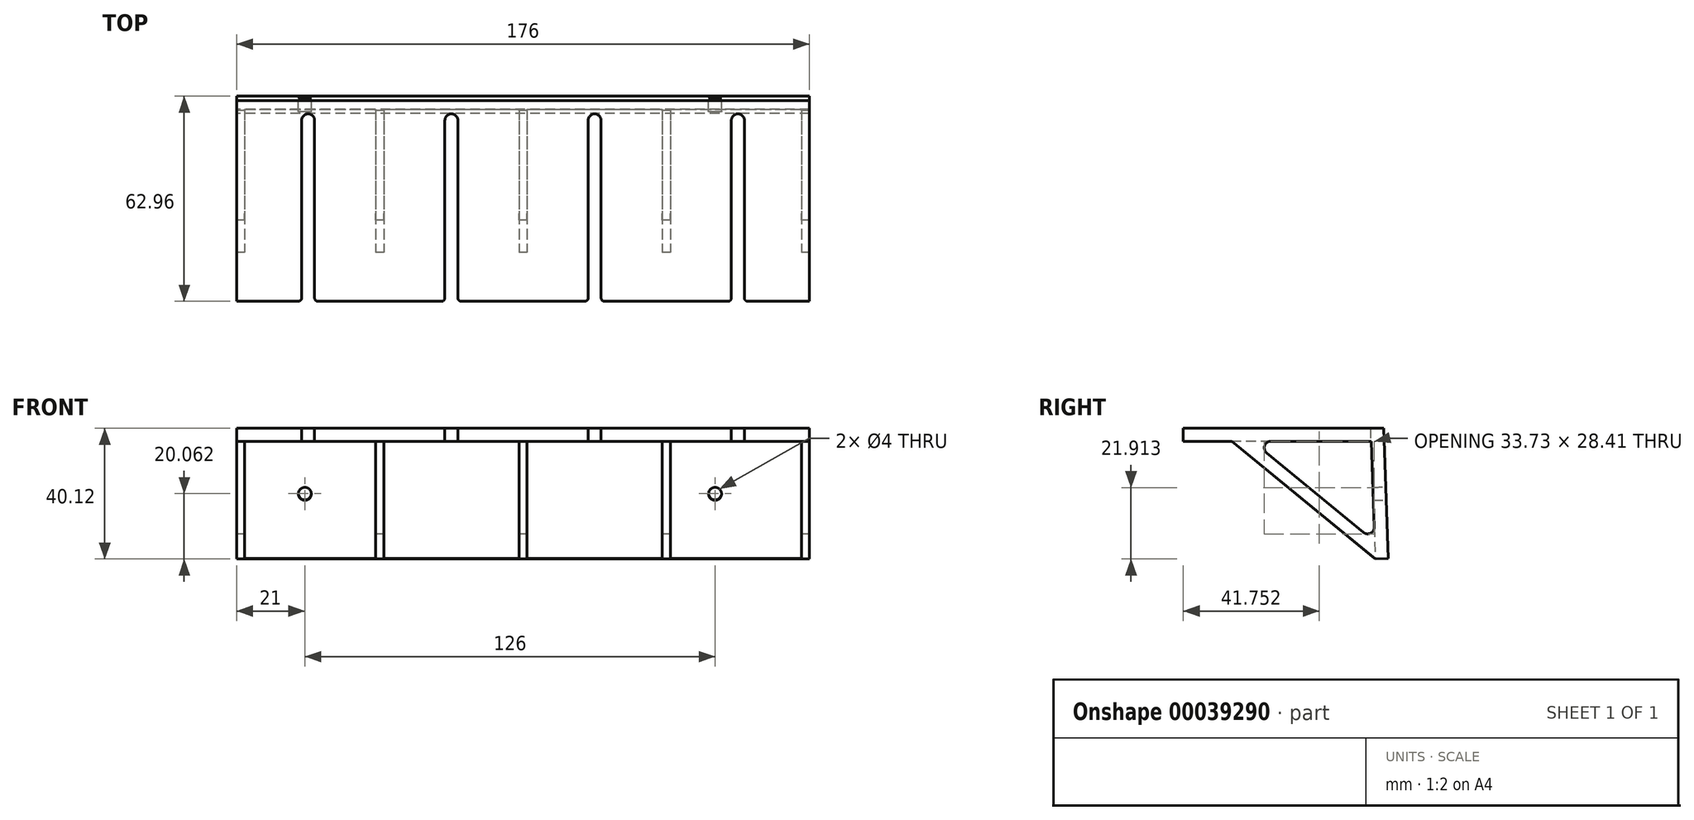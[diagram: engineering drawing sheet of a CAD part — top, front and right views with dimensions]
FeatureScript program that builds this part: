
annotation { "Feature Type Name" : "Feature", "Feature Type Description" : "" }
export const myFeature = defineFeature(function(context is Context, id is Id, definition is map)
    precondition{}
    {
        {
            var Q0;
            Q0=qCreatedBy(makeId("Top.planeOp"),FACE);
            var sketch = newSketch(context, id + "F0", { "sketchPlane" : qUnion([Q0])});
            skLineSegment(sketch, "E0", {"start": v(0, 0) * mm, "end": v(176, 0) * mm});
            skLineSegment(sketch, "E1", {"start": v(0, 0) * mm, "end": v(0, -61.56) * mm});
            skLineSegment(sketch, "E2", {"start": v(0, -61.56) * mm, "end": v(19, -61.56) * mm});
            skLineSegment(sketch, "E3", {"start": v(20, -60.56) * mm, "end": v(20, -6) * mm});
            skLineSegment(sketch, "E4", {"start": v(24, -6) * mm, "end": v(24, -60.56) * mm});
            skLineSegment(sketch, "E5", {"start": v(25, -61.56) * mm, "end": v(63, -61.56) * mm});
            skLineSegment(sketch, "E6", {"start": v(64, -60.56) * mm, "end": v(64, -6) * mm});
            skLineSegment(sketch, "E7", {"start": v(68, -6) * mm, "end": v(68, -60.56) * mm});
            skLineSegment(sketch, "E8", {"start": v(69, -61.56) * mm, "end": v(107, -61.56) * mm});
            skLineSegment(sketch, "E9", {"start": v(108, -60.56) * mm, "end": v(108, -6) * mm});
            skLineSegment(sketch, "E10", {"start": v(112, -6) * mm, "end": v(112, -60.56) * mm});
            skLineSegment(sketch, "E11", {"start": v(113, -61.56) * mm, "end": v(151, -61.56) * mm});
            skLineSegment(sketch, "E12", {"start": v(152, -60.56) * mm, "end": v(152, -6) * mm});
            skLineSegment(sketch, "E13", {"start": v(156, -6) * mm, "end": v(156, -60.56) * mm});
            skArc(sketch, "E14", {"start": v(20, -6) * mm, "mid": v(22, -4) * mm, "end": v(24, -6) * mm});
            skArc(sketch, "E15", {"start": v(64, -6) * mm, "mid": v(66, -4) * mm, "end": v(68, -6) * mm});
            skArc(sketch, "E16", {"start": v(108, -6) * mm, "mid": v(110, -4) * mm, "end": v(112, -6) * mm});
            skArc(sketch, "E17", {"start": v(152, -6) * mm, "mid": v(154, -4) * mm, "end": v(156, -6) * mm});
            skLineSegment(sketch, "E18", {"start": v(22, -6) * mm, "end": v(154, -6) * mm, "construction": true});
            skPoint(sketch, "E19.visualSharp", {"position": v(64, -61.56) * mm});
            skArc(sketch, "E19.filletArc", {"start": v(63, -61.56) * mm, "mid": v(63.7, -61.27) * mm, "end": v(64, -60.56) * mm});
            skPoint(sketch, "E20.visualSharp", {"position": v(20, -61.56) * mm});
            skArc(sketch, "E20.filletArc", {"start": v(19, -61.56) * mm, "mid": v(19.7, -61.27) * mm, "end": v(20, -60.56) * mm});
            skPoint(sketch, "E21.visualSharp", {"position": v(24, -61.56) * mm});
            skArc(sketch, "E21.filletArc", {"start": v(24, -60.56) * mm, "mid": v(24.3, -61.27) * mm, "end": v(25, -61.56) * mm});
            skPoint(sketch, "E22.visualSharp", {"position": v(68, -61.56) * mm});
            skArc(sketch, "E22.filletArc", {"start": v(68, -60.56) * mm, "mid": v(68.3, -61.27) * mm, "end": v(69, -61.56) * mm});
            skPoint(sketch, "E23.visualSharp", {"position": v(108, -61.56) * mm});
            skArc(sketch, "E23.filletArc", {"start": v(107, -61.56) * mm, "mid": v(107.7, -61.27) * mm, "end": v(108, -60.56) * mm});
            skPoint(sketch, "E24.visualSharp", {"position": v(112, -61.56) * mm});
            skArc(sketch, "E24.filletArc", {"start": v(112, -60.56) * mm, "mid": v(112.3, -61.27) * mm, "end": v(113, -61.56) * mm});
            skPoint(sketch, "E25.visualSharp", {"position": v(152, -61.56) * mm});
            skArc(sketch, "E25.filletArc", {"start": v(151, -61.56) * mm, "mid": v(151.7, -61.27) * mm, "end": v(152, -60.56) * mm});
            skLineSegment(sketch, "E26", {"start": v(157, -61.56) * mm, "end": v(176, -61.56) * mm});
            skLineSegment(sketch, "E27", {"start": v(176, -61.56) * mm, "end": v(176, 0) * mm});
            skPoint(sketch, "E28.visualSharp", {"position": v(156, -61.56) * mm});
            skArc(sketch, "E28.filletArc", {"start": v(156, -60.56) * mm, "mid": v(156.3, -61.27) * mm, "end": v(157, -61.56) * mm});
            skSolve(sketch);
        }
        {
            var Q0;
            Q0=makeQuery(id+"F0.imprint","IMPRINT",FACE,{"disambiguationData":[TD([[makeQuery(id+"F0.imprint","IMPRINT",EDGE,{"derivedFrom":sQuery(id+"F0.wireOp",EDGE,"E0")}),-1.0]])]});
            extrude(context, id + "F1", {"entities" : qUnion([Q0]), "depth" : 4 * mm});
        }
        {
            var Q0;
            Q0=makeQuery(id+"F1.opExtrude","SWEPT_FACE",FACE,{"disambiguationData":[OSD([sQuery(id+"F0.wireOp",EDGE,"E0")])]});
            var sketch = newSketch(context, id + "F2", { "sketchPlane" : qUnion([Q0])});
            skLineSegment(sketch, "E29", {"start": v(0, 4) * mm, "end": v(0, -100) * mm});
            skLineSegment(sketch, "E30", {"start": v(0, -100) * mm, "end": v(-44, -100) * mm});
            skLineSegment(sketch, "E31", {"start": v(-44, -110) * mm, "end": v(-44, -100) * mm});
            skLineSegment(sketch, "E32", {"start": v(-44, -110) * mm, "end": v(-88, -110) * mm});
            skLineSegment(sketch, "E33", {"start": v(-88, -135) * mm, "end": v(-88, -110) * mm});
            skLineSegment(sketch, "E34", {"start": v(-88, -135) * mm, "end": v(-132, -135) * mm});
            skLineSegment(sketch, "E35", {"start": v(-132, -155) * mm, "end": v(-132, -135) * mm});
            skLineSegment(sketch, "E36", {"start": v(-132, -155) * mm, "end": v(-176, -155) * mm});
            skLineSegment(sketch, "E37", {"start": v(-176, -155) * mm, "end": v(-176, -22) * mm});
            skLineSegment(sketch, "E38", {"start": v(-154, 4) * mm, "end": v(-154, -155) * mm, "construction": true});
            skLineSegment(sketch, "E39", {"start": v(-110, -135) * mm, "end": v(-110, 4) * mm, "construction": true});
            skLineSegment(sketch, "E40", {"start": v(-66, -110) * mm, "end": v(-66, 4) * mm, "construction": true});
            skLineSegment(sketch, "E41", {"start": v(-22, -100) * mm, "end": v(-22, 4) * mm, "construction": true});
            skLineSegment(sketch, "E42", {"start": v(-22, -48.08) * mm, "end": v(-66, -48.08) * mm, "construction": true});
            skLineSegment(sketch, "E43", {"start": v(-66, -48.08) * mm, "end": v(-110, -48.08) * mm, "construction": true});
            skLineSegment(sketch, "E44", {"start": v(-110, -48.08) * mm, "end": v(-154, -48.08) * mm, "construction": true});
            skLineSegment(sketch, "E45", {"start": v(-132, -135) * mm, "end": v(-132, -48.08) * mm, "construction": true});
            skLineSegment(sketch, "E46", {"start": v(-88, -110) * mm, "end": v(-88, -48.08) * mm, "construction": true});
            skLineSegment(sketch, "E47", {"start": v(-44, -100) * mm, "end": v(-44, -48.08) * mm, "construction": true});
            skLineSegment(sketch, "E48", {"start": v(0, 4) * mm, "end": v(-176, 4) * mm});
            skLineSegment(sketch, "E49", {"start": v(-176, 4) * mm, "end": v(-304, 4) * mm});
            skLineSegment(sketch, "E50", {"start": v(-304, 4) * mm, "end": v(-304, -22) * mm});
            skLineSegment(sketch, "E51", {"start": v(-304, -22) * mm, "end": v(-176, -22) * mm});
            skCircle(sketch, "E52", {"center": v(-195, -9) * mm, "radius": 9 * mm});
            skCircle(sketch, "E53", {"center": v(-243, -9) * mm, "radius": 9 * mm});
            skCircle(sketch, "E54", {"center": v(-291, -9) * mm, "radius": 9 * mm});
            skLineSegment(sketch, "E55", {"start": v(-195, -9) * mm, "end": v(-291, -9) * mm, "construction": true});
            skLineSegment(sketch, "E56", {"start": v(-291, -9) * mm, "end": v(-304, -9) * mm, "construction": true});
            skLineSegment(sketch, "E57", {"start": v(-176, -22) * mm, "end": v(-176, 4) * mm});
            skSolve(sketch);
        }
        {
            var Q0;
            Q0=makeQuery(id+"F1.opExtrude","SWEPT_FACE",FACE,{"disambiguationData":[OSD([sQuery(id+"F0.wireOp",EDGE,"E1")])]});
            var sketch = newSketch(context, id + "F3", { "sketchPlane" : qUnion([Q0])});
            skLineSegment(sketch, "E58", {"start": v(3.86, 0) * mm, "end": v(34.67, 0) * mm});
            skLineSegment(sketch, "E59", {"start": v(0, 4) * mm, "end": v(-1.4, -35.98) * mm});
            skLineSegment(sketch, "E60", {"start": v(2.94, -26.36) * mm, "end": v(3.86, 0) * mm});
            skLineSegment(sketch, "E61", {"start": v(0, 4) * mm, "end": v(4, 4) * mm});
            skLineSegment(sketch, "E62", {"start": v(2.6, -36.12) * mm, "end": v(-1.4, -35.98) * mm});
            skLineSegment(sketch, "E63", {"start": v(46.56, 0) * mm, "end": v(2.6, -36.12) * mm});
            skLineSegment(sketch, "E64.0", {"start": v(35.94, -3.55) * mm, "end": v(6.21, -27.97) * mm});
            skPoint(sketch, "E65.visualSharp", {"position": v(2.79, -30.79) * mm});
            skArc(sketch, "E65.filletArc", {"start": v(2.94, -26.36) * mm, "mid": v(4.06, -28.22) * mm, "end": v(6.21, -27.97) * mm});
            skPoint(sketch, "E66.visualSharp", {"position": v(40.26, 0) * mm});
            skArc(sketch, "E66.filletArc", {"start": v(35.94, -3.55) * mm, "mid": v(36.56, -1.33) * mm, "end": v(34.67, 0) * mm});
            skPoint(sketch, "E67.visualSharp", {"position": v(3.86, 0) * mm});
            skSolve(sketch);
        }
        {
            var Q0;
            Q0=makeQuery(id+"F3.imprint","IMPRINT",FACE,{"disambiguationData":[TD([[makeQuery(id+"F3.imprint","IMPRINT",EDGE,{"derivedFrom":sQuery(id+"F3.wireOp",EDGE,"E59")}),1.0]])]});
            var Q1;
            Q1=makeQuery(id+"F3.imprint","IMPRINT",FACE,{"disambiguationData":[TD([[makeQuery(id+"F3.imprint","IMPRINT",EDGE,{"derivedFrom":sQuery(id+"F3.wireOp",EDGE,"c7156f05-824d-4470-9329-524be284baaa")}),-1.0]])]});
            var Q2;
            Q2=makeQuery(id+"F1.opExtrude","SWEPT_FACE",FACE,{"disambiguationData":[OSD([sQuery(id+"F0.wireOp",EDGE,"E27")])]});
            extrude(context, id + "F4", {"entities" : qUnion([Q0, Q1]), "operationType" : NewBodyOperationType.ADD, "endBound" : BoundingType.UP_TO_SURFACE, "oppositeDirection" : true, "endBoundEntityFace" : qUnion([Q2]), "depth" : 2.5 * mm});
        }
        {
            var Q0;
            Q0=makeQuery(id+"F4.opExtrude","SWEPT_FACE",FACE,{"disambiguationData":[OSD([sQuery(id+"F3.wireOp",EDGE,"E59")])]});
            cPlane(context, id + "F5", {"entities" : qUnion([Q0]), "cplaneType" : CPlaneType.OFFSET, "offset" : 4 * mm, "oppositeDirection" : true, "width" : 150 * mm, "height" : 150 * mm});
        }
        {
            var Q0;
            Q0=makeQuery(id+"F1.opExtrude","SWEPT_FACE",FACE,{"disambiguationData":[OSD([sQuery(id+"F0.wireOp",EDGE,"E2")])]});
            var sketch = newSketch(context, id + "F6", { "sketchPlane" : qUnion([Q0])});
            skLineSegment(sketch, "E68.bottom", {"start": v(2.5, 0) * mm, "end": v(42.75, 0) * mm});
            skLineSegment(sketch, "E68.top", {"start": v(2.5, -35.98) * mm, "end": v(42.75, -35.98) * mm});
            skLineSegment(sketch, "E68.left", {"start": v(2.5, 0) * mm, "end": v(2.5, -35.98) * mm});
            skLineSegment(sketch, "E68.right", {"start": v(42.75, 0) * mm, "end": v(42.75, -35.98) * mm});
            skLineSegment(sketch, "E69.bottom", {"start": v(45.25, 0) * mm, "end": v(86.75, 0) * mm});
            skLineSegment(sketch, "E69.top", {"start": v(45.25, -35.98) * mm, "end": v(86.75, -35.98) * mm});
            skLineSegment(sketch, "E69.left", {"start": v(45.25, 0) * mm, "end": v(45.25, -35.98) * mm});
            skLineSegment(sketch, "E69.right", {"start": v(86.75, 0) * mm, "end": v(86.75, -35.98) * mm});
            skLineSegment(sketch, "E70.bottom", {"start": v(89.25, 0) * mm, "end": v(130.75, 0) * mm});
            skLineSegment(sketch, "E70.top", {"start": v(89.25, -35.98) * mm, "end": v(130.75, -35.98) * mm});
            skLineSegment(sketch, "E70.left", {"start": v(89.25, 0) * mm, "end": v(89.25, -35.98) * mm});
            skLineSegment(sketch, "E70.right", {"start": v(130.75, 0) * mm, "end": v(130.75, -35.98) * mm});
            skLineSegment(sketch, "E71.bottom", {"start": v(133.25, 0) * mm, "end": v(173.5, 0) * mm});
            skLineSegment(sketch, "E71.top", {"start": v(133.25, -35.98) * mm, "end": v(173.5, -35.98) * mm});
            skLineSegment(sketch, "E71.left", {"start": v(133.25, 0) * mm, "end": v(133.25, -35.98) * mm});
            skLineSegment(sketch, "E71.right", {"start": v(173.5, 0) * mm, "end": v(173.5, -35.98) * mm});
            skLineSegment(sketch, "E72", {"start": v(42.75, -35.98) * mm, "end": v(45.25, -35.98) * mm, "construction": true});
            skLineSegment(sketch, "E73", {"start": v(86.75, -35.98) * mm, "end": v(89.25, -35.98) * mm, "construction": true});
            skLineSegment(sketch, "E74", {"start": v(130.75, -35.98) * mm, "end": v(133.25, -35.98) * mm, "construction": true});
            skLineSegment(sketch, "E75", {"start": v(44, -35.98) * mm, "end": v(44, -100) * mm, "construction": true});
            skSolve(sketch);
        }
        {
            var Q0;
            {Q0=qUnion([makeQuery(id+"F6.imprint","IMPRINT",FACE,{"disambiguationData":[TD([[makeQuery(id+"F6.imprint","IMPRINT",EDGE,{"derivedFrom":sQuery(id+"F6.wireOp",EDGE,"E71.bottom")}),-1.0]])]}),makeQuery(id+"F6.imprint","IMPRINT",FACE,{"disambiguationData":[TD([[makeQuery(id+"F6.imprint","IMPRINT",EDGE,{"derivedFrom":sQuery(id+"F6.wireOp",EDGE,"E70.bottom")}),-1.0]])]}),makeQuery(id+"F6.imprint","IMPRINT",FACE,{"disambiguationData":[TD([[makeQuery(id+"F6.imprint","IMPRINT",EDGE,{"derivedFrom":sQuery(id+"F6.wireOp",EDGE,"E69.bottom")}),-1.0]])]}),makeQuery(id+"F6.imprint","IMPRINT",FACE,{"disambiguationData":[TD([[makeQuery(id+"F6.imprint","IMPRINT",EDGE,{"derivedFrom":sQuery(id+"F6.wireOp",EDGE,"E68.top")}),1.0]])]})]);}
            var Q1;
            Q1=qCreatedBy(id+"F5.planeOp",FACE);
            extrude(context, id + "F7", {"entities" : qUnion([Q0]), "operationType" : NewBodyOperationType.REMOVE, "endBound" : BoundingType.UP_TO_SURFACE, "oppositeDirection" : true, "endBoundEntityFace" : qUnion([Q1]), "depth" : 25 * mm});
        }
        {
            var Q0;
            Q0=makeQuery(id+"F4.opExtrude","SWEPT_FACE",FACE,{"disambiguationData":[OSD([sQuery(id+"F3.wireOp",EDGE,"E59")])]});
            var sketch = newSketch(context, id + "F8", { "sketchPlane" : qUnion([Q0])});
            skCircle(sketch, "E76", {"center": v(-147, -16) * mm, "radius": 2 * mm});
            skCircle(sketch, "E77", {"center": v(-21, -16) * mm, "radius": 2 * mm});
            skSolve(sketch);
        }
        {
            var Q0;
            Q0 = qSketchRegion(id + "F8", true);
            extrude(context, id + "F9", {"entities" : qUnion([Q0]), "operationType" : NewBodyOperationType.REMOVE, "oppositeDirection" : true, "depth" : 25 * mm});
        }
    });
